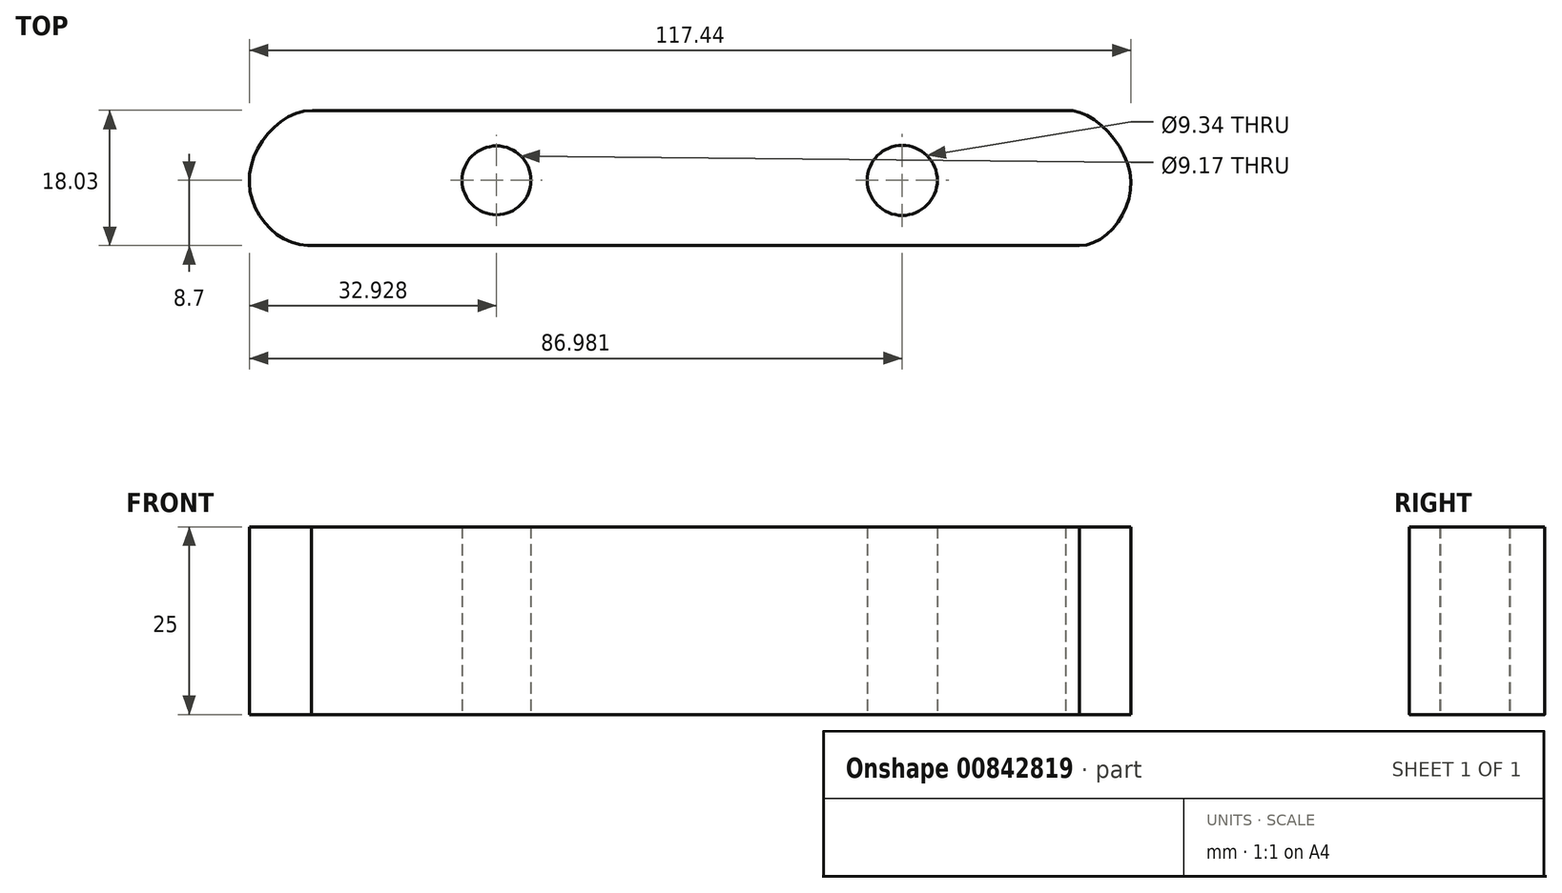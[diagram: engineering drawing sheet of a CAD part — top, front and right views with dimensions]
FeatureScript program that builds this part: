
annotation { "Feature Type Name" : "Feature", "Feature Type Description" : "" }
export const myFeature = defineFeature(function(context is Context, id is Id, definition is map)
    precondition{}
    {
        {
            var Q0;
            Q0=qCreatedBy(makeId("Top.planeOp"),FACE);
            var sketch = newSketch(context, id + "F0", { "sketchPlane" : qUnion([Q0])});
            skLineSegment(sketch, "E0", {"start": v(-32.77, 9.32) * mm, "end": v(67.57, 9.32) * mm});
            skLineSegment(sketch, "E1", {"start": v(-33.4, -8.7) * mm, "end": v(69.43, -8.7) * mm});
            skFitSpline(sketch, "E2", {"points": [v(67.57, 9.32) * mm, v(76.26, 0) * mm, v(69.43, -8.7) * mm, v(62.29, 0) * mm, v(67.57, 9.32) * mm]});
            skFitSpline(sketch, "E3", {"points": [v(-32.77, 9.32) * mm, v(-41.16, 0) * mm, v(-33.4, -8.7) * mm, v(-23.76, 0) * mm, v(-32.77, 9.32) * mm]});
            skCircle(sketch, "E4", {"center": v(-8.23, 0) * mm, "radius": 4.59 * mm});
            skCircle(sketch, "E5", {"center": v(45.82, 0) * mm, "radius": 4.67 * mm});
            skSolve(sketch);
        }
        {
            var Q0;
            Q0 = qSketchRegion(id + "F0", true);
            extrude(context, id + "F1", {"entities" : qUnion([Q0]), "depth" : 25 * mm, "offsetDistance" : 25 * mm});
        }
    });
